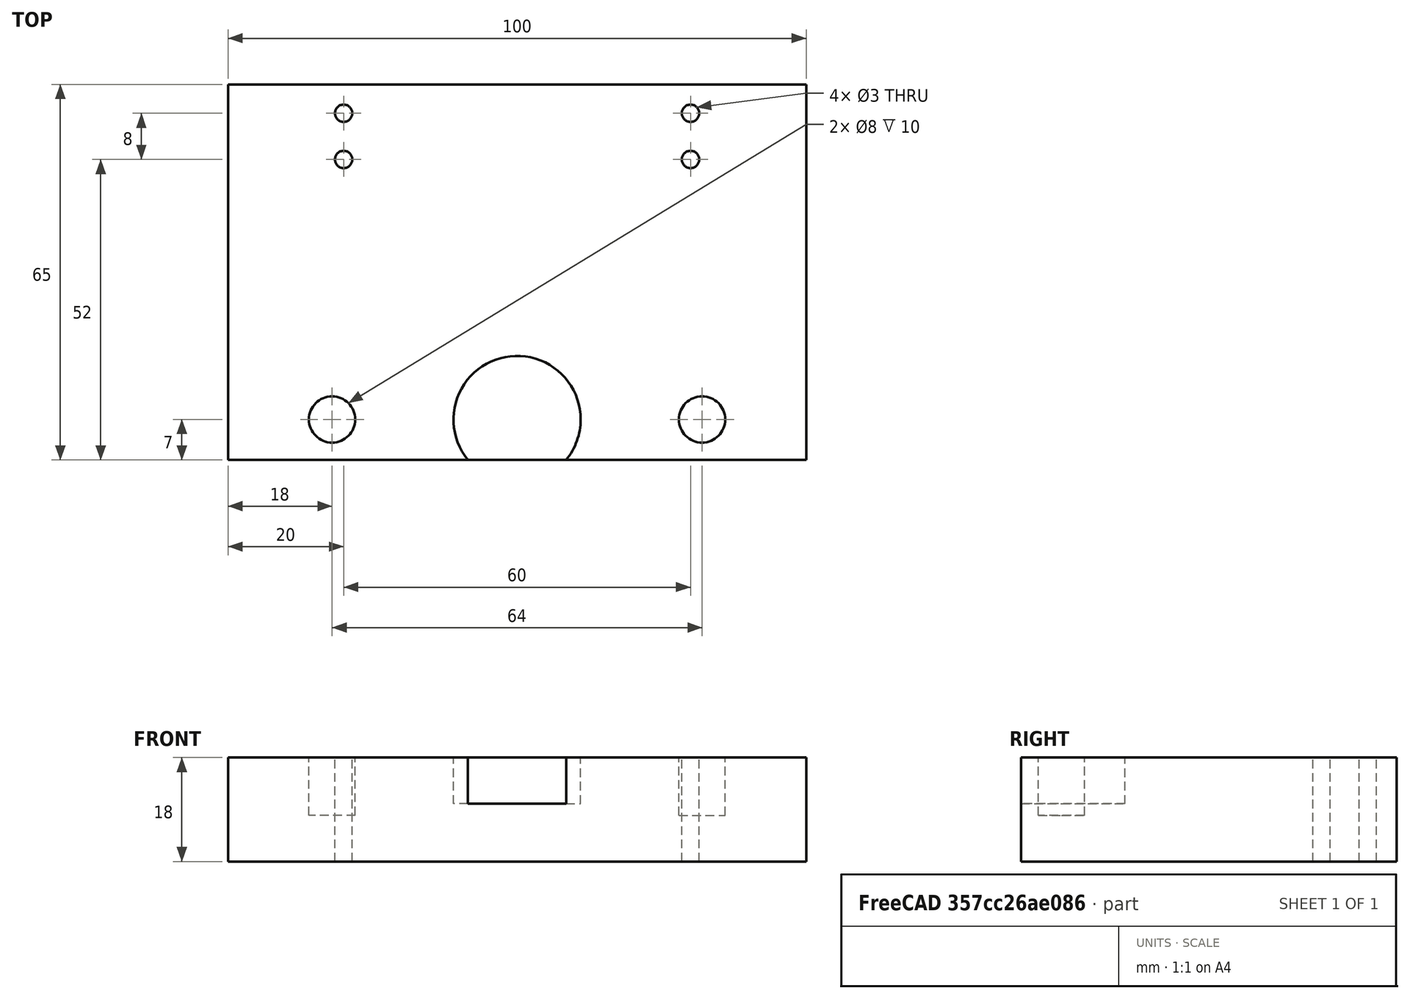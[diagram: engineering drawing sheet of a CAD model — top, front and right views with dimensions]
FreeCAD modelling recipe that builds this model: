
FCSTD DOCUMENT  (FreeCAD 0.17R13541 (Git))
Label: Z-Abajo
License: All rights reserved
LicenseURL: http://en.wikipedia.org/wiki/All_rights_reserved
objects: Part::Cylinder×4, Part::MultiFuse×2, Part::Cut×2, Part::Box×1, Part::Mirroring×1
note: 10 computed .brp shape members not serialized (recipe doc carries the construction recipe); baked Part::Feature solids carry a one-line shape summary decoded from their .brp

FEATURE [Part::Box] Box  label="Cubo"
  AttacherType = Attacher::AttachEngine3D
  Height = 18
  Length = 50
  Width = 65
FEATURE [Part::Cylinder] Cylinder  label="Cilindro"
  Angle = 360
  AttacherType = Attacher::AttachEngine3D
  Height = 25
  Placement = pos=(18,7,8) rot=(0,0,1;0rad)
  Radius = 4
FEATURE [Part::Cylinder] Cylinder001  label="Cilindro001"
  Angle = 360
  AttacherType = Attacher::AttachEngine3D
  Height = 25
  Placement = pos=(20,52,0) rot=(0,0,1;0rad)
  Radius = 1.5
FEATURE [Part::Cylinder] Cylinder002  label="Cilindro002"
  Angle = 360
  AttacherType = Attacher::AttachEngine3D
  Height = 25
  Placement = pos=(20,60,0) rot=(0,0,1;0rad)
  Radius = 1.5
FEATURE [Part::MultiFuse] Fusion
  Refine = true
  Shapes = -> [Cylinder002,Cylinder001,Cylinder]
FEATURE [Part::Cut] Cut  label="Izquierda"
  Base = -> Box
  Refine = true
  Tool = -> Fusion
FEATURE [Part::Mirroring] mirror  label="Mirror of Izquierda"
  Base = (50,0,0)
  Normal = (0.71,0,0)
  Source = -> Cut
FEATURE [Part::Cylinder] Cylinder003  label="Cilindro003"
  Angle = 360
  AttacherType = Attacher::AttachEngine3D
  Height = 15
  Placement = pos=(50,7,10) rot=(0,0,1;0rad)
  Radius = 11
FEATURE [Part::MultiFuse] Fusion001
  Refine = true
  Shapes = -> [mirror,Cut]
FEATURE [Part::Cut] Cut001  label="Z-Abajo"
  Base = -> Fusion001
  Refine = true
  Tool = -> Cylinder003
